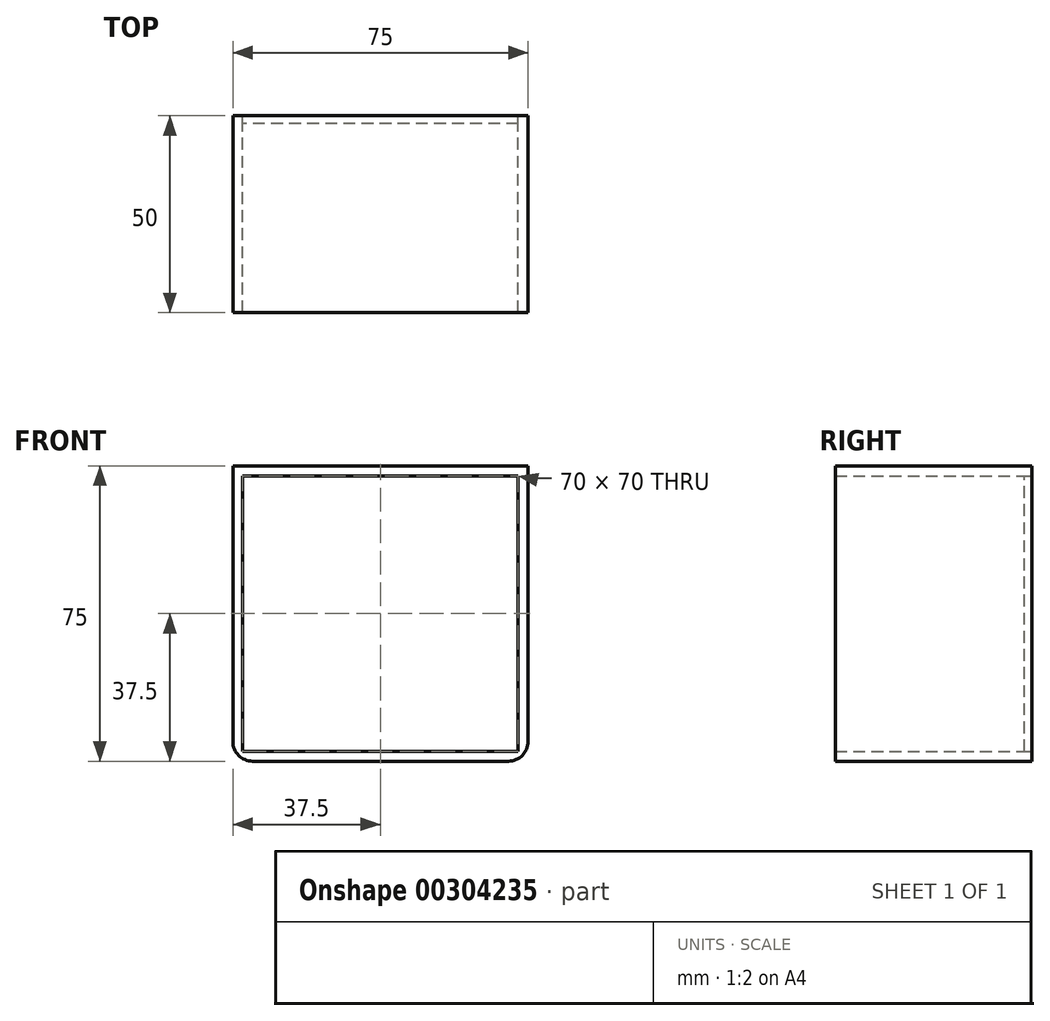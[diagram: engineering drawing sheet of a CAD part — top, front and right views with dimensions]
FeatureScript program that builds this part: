
annotation { "Feature Type Name" : "Feature", "Feature Type Description" : "" }
export const myFeature = defineFeature(function(context is Context, id is Id, definition is map)
    precondition{}
    {
        {
            var Q0;
            Q0=qCreatedBy(makeId("Front.planeOp"),FACE);
            var sketch = newSketch(context, id + "F0", { "sketchPlane" : qUnion([Q0])});
            skLineSegment(sketch, "E0.bottom", {"start": v(37.5, -37.5) * mm, "end": v(-37.5, -37.5) * mm});
            skLineSegment(sketch, "E0.top", {"start": v(37.5, 37.5) * mm, "end": v(-37.5, 37.5) * mm});
            skLineSegment(sketch, "E0.left", {"start": v(37.5, -37.5) * mm, "end": v(37.5, 37.5) * mm});
            skLineSegment(sketch, "E0.right", {"start": v(-37.5, -37.5) * mm, "end": v(-37.5, 37.5) * mm});
            skPoint(sketch, "E0.middle", {"position": v(0, 0) * mm});
            skLineSegment(sketch, "E1.bottom", {"start": v(35, -35) * mm, "end": v(-35, -35) * mm});
            skLineSegment(sketch, "E1.top", {"start": v(35, 35) * mm, "end": v(-35, 35) * mm});
            skLineSegment(sketch, "E1.left", {"start": v(35, -35) * mm, "end": v(35, 35) * mm});
            skLineSegment(sketch, "E1.right", {"start": v(-35, -35) * mm, "end": v(-35, 35) * mm});
            skSolve(sketch);
        }
        {
            var Q0;
            Q0 = qSketchRegion(id + "F0", true);
            extrude(context, id + "F1", {"entities" : qUnion([Q0]), "endBound" : BoundingType.SYMMETRIC, "depth" : 50 * mm});
        }
        {
            var Q0;
            Q0=makeQuery(id+"F1.opExtrude","SWEPT_EDGE",EDGE,{"disambiguationData":[OSD([sQuery(id+"F0.wireOp",EDGE,"E0.bottom"),sQuery(id+"F0.wireOp",EDGE,"E0.right")])]});
            var Q1;
            Q1=makeQuery(id+"F1.opExtrude","SWEPT_EDGE",EDGE,{"disambiguationData":[OSD([sQuery(id+"F0.wireOp",EDGE,"E0.bottom"),sQuery(id+"F0.wireOp",EDGE,"E0.left")])]});
            fillet(context, id + "F2", {"entities" : qUnion([Q0, Q1]), "radius" : 5 * mm, "tangentPropagation" : true, "allowEdgeOverflow" : false});
        }
        {
            var Q0;
            Q0=makeQuery(id+"F1.opExtrude","CAP_FACE",FACE,{"disambiguationData":[OSD([sQuery(id+"F0.wireOp",EDGE,"E0.bottom"),sQuery(id+"F0.wireOp",EDGE,"E0.top"),sQuery(id+"F0.wireOp",EDGE,"E0.left"),sQuery(id+"F0.wireOp",EDGE,"E0.right"),sQuery(id+"F0.wireOp",EDGE,"E1.bottom"),sQuery(id+"F0.wireOp",EDGE,"E1.top"),sQuery(id+"F0.wireOp",EDGE,"E1.left"),sQuery(id+"F0.wireOp",EDGE,"E1.right")])],"isStart":true});
            var sketch = newSketch(context, id + "F3", { "sketchPlane" : qUnion([Q0])});
            skLineSegment(sketch, "E2.0", {"start": v(35, -35) * mm, "end": v(35, 35) * mm});
            skLineSegment(sketch, "E3.0", {"start": v(-35, -35) * mm, "end": v(35, -35) * mm});
            skLineSegment(sketch, "E4.0", {"start": v(-35, -35) * mm, "end": v(-35, 35) * mm});
            skLineSegment(sketch, "E5.0", {"start": v(-35, 35) * mm, "end": v(35, 35) * mm});
            skSolve(sketch);
        }
        {
            var Q0;
            Q0 = qSketchRegion(id + "F3", true);
            extrude(context, id + "F4", {"entities" : qUnion([Q0]), "oppositeDirection" : true, "depth" : 2 * mm});
        }
    });
